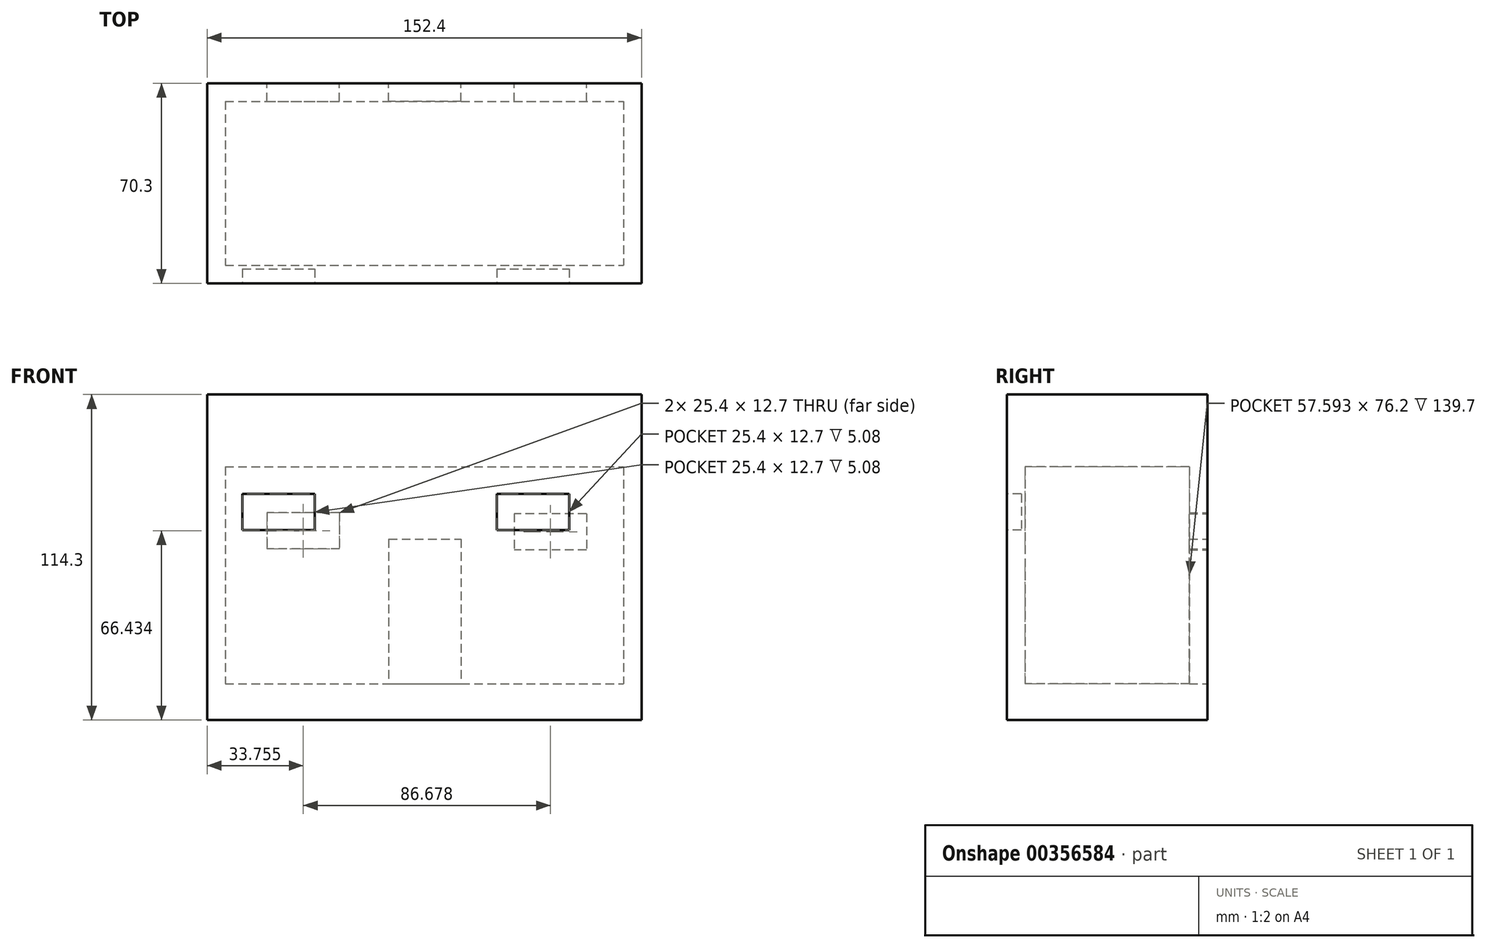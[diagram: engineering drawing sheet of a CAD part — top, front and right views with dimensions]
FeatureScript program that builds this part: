
annotation { "Feature Type Name" : "Feature", "Feature Type Description" : "" }
export const myFeature = defineFeature(function(context is Context, id is Id, definition is map)
    precondition{}
    {
        {
            var Q0;
            Q0=qCreatedBy(makeId("Top.planeOp"),FACE);
            var sketch = newSketch(context, id + "F0", { "sketchPlane" : qUnion([Q0])});
            skLineSegment(sketch, "E0.bottom", {"start": v(76.2, 35.15) * mm, "end": v(-76.2, 35.15) * mm});
            skLineSegment(sketch, "E0.top", {"start": v(76.2, -35.15) * mm, "end": v(-76.2, -35.15) * mm});
            skLineSegment(sketch, "E0.left", {"start": v(76.2, 35.15) * mm, "end": v(76.2, -35.15) * mm});
            skLineSegment(sketch, "E0.right", {"start": v(-76.2, 35.15) * mm, "end": v(-76.2, -35.15) * mm});
            skPoint(sketch, "E0.middle", {"position": v(0, 0) * mm});
            skSolve(sketch);
        }
        {
            var Q0;
            Q0 = qSketchRegion(id + "F0", true);
            extrude(context, id + "F1", {"entities" : qUnion([Q0]), "depth" : 12.7 * mm});
        }
        {
            var Q0;
            Q0=makeQuery(id+"F1.opExtrude","CAP_FACE",FACE,{"disambiguationData":[OSD([sQuery(id+"F0.wireOp",EDGE,"E0.bottom"),sQuery(id+"F0.wireOp",EDGE,"E0.top"),sQuery(id+"F0.wireOp",EDGE,"E0.left"),sQuery(id+"F0.wireOp",EDGE,"E0.right")])],"isStart":false});
            var sketch = newSketch(context, id + "F2", { "sketchPlane" : qUnion([Q0])});
            skLineSegment(sketch, "E1.bottom", {"start": v(-76.2, 35.15) * mm, "end": v(76.2, 35.15) * mm});
            skLineSegment(sketch, "E1.top", {"start": v(-76.2, 28.8) * mm, "end": v(76.2, 28.8) * mm});
            skLineSegment(sketch, "E1.left", {"start": v(-76.2, 35.15) * mm, "end": v(-76.2, 28.8) * mm});
            skLineSegment(sketch, "E1.right", {"start": v(76.2, 35.15) * mm, "end": v(76.2, 28.8) * mm});
            skLineSegment(sketch, "E2.bottom", {"start": v(-76.2, -28.8) * mm, "end": v(76.2, -28.8) * mm});
            skLineSegment(sketch, "E2.top", {"start": v(-76.2, -35.15) * mm, "end": v(76.2, -35.15) * mm});
            skLineSegment(sketch, "E2.left", {"start": v(-76.2, -28.8) * mm, "end": v(-76.2, -35.15) * mm});
            skLineSegment(sketch, "E2.right", {"start": v(76.2, -28.8) * mm, "end": v(76.2, -35.15) * mm});
            skLineSegment(sketch, "E3.bottom", {"start": v(-70.56, 35.15) * mm, "end": v(-63.18, 35.15) * mm});
            skLineSegment(sketch, "E4.bottom", {"start": v(-76.2, 28.8) * mm, "end": v(-69.85, 28.8) * mm});
            skLineSegment(sketch, "E4.top", {"start": v(-76.2, -28.8) * mm, "end": v(-69.85, -28.8) * mm});
            skLineSegment(sketch, "E4.left", {"start": v(-76.2, 28.8) * mm, "end": v(-76.2, -28.8) * mm});
            skLineSegment(sketch, "E4.right", {"start": v(-69.85, 28.8) * mm, "end": v(-69.85, -28.8) * mm});
            skLineSegment(sketch, "E5.bottom", {"start": v(76.2, 28.8) * mm, "end": v(69.85, 28.8) * mm});
            skLineSegment(sketch, "E5.top", {"start": v(76.2, -28.8) * mm, "end": v(69.85, -28.8) * mm});
            skLineSegment(sketch, "E5.left", {"start": v(76.2, 28.8) * mm, "end": v(76.2, -28.8) * mm});
            skLineSegment(sketch, "E5.right", {"start": v(69.85, 28.8) * mm, "end": v(69.85, -28.8) * mm});
            skSolve(sketch);
        }
        {
            var Q0;
            Q0 = qSketchRegion(id + "F2", true);
            extrude(context, id + "F3", {"entities" : qUnion([Q0]), "operationType" : NewBodyOperationType.ADD, "depth" : 76.2 * mm});
        }
        {
            var Q0;
            Q0=makeQuery(id+"F3.boolean.opBoolean","MERGE",FACE,{"derivedFrom":[makeQuery(id+"F1.opExtrude","SWEPT_FACE",FACE,{"disambiguationData":[OSD([sQuery(id+"F0.wireOp",EDGE,"E0.bottom")])]}),makeQuery(id+"F3.opExtrude","SWEPT_FACE",FACE,{"disambiguationData":[OSD([sQuery(id+"F2.wireOp",EDGE,"E1.bottom"),sQuery(id+"F2.wireOp",EDGE,"E3.bottom")])]})]});
            var sketch = newSketch(context, id + "F4", { "sketchPlane" : qUnion([Q0])});
            skLineSegment(sketch, "E6.bottom", {"start": v(12.47, 63.5) * mm, "end": v(-12.93, 63.5) * mm});
            skLineSegment(sketch, "E6.top", {"start": v(12.47, 12.7) * mm, "end": v(-12.93, 12.7) * mm});
            skLineSegment(sketch, "E6.left", {"start": v(12.47, 63.5) * mm, "end": v(12.47, 12.7) * mm});
            skLineSegment(sketch, "E6.right", {"start": v(-12.93, 63.5) * mm, "end": v(-12.93, 12.7) * mm});
            skLineSegment(sketch, "E7.bottom", {"start": v(-56.93, 72.46) * mm, "end": v(-31.53, 72.46) * mm});
            skLineSegment(sketch, "E7.top", {"start": v(-56.93, 59.76) * mm, "end": v(-31.53, 59.76) * mm});
            skLineSegment(sketch, "E7.left", {"start": v(-56.93, 72.46) * mm, "end": v(-56.93, 59.76) * mm});
            skLineSegment(sketch, "E7.right", {"start": v(-31.53, 72.46) * mm, "end": v(-31.53, 59.76) * mm});
            skLineSegment(sketch, "E8.bottom", {"start": v(29.75, 72.78) * mm, "end": v(55.15, 72.78) * mm});
            skLineSegment(sketch, "E8.top", {"start": v(29.75, 60.08) * mm, "end": v(55.15, 60.08) * mm});
            skLineSegment(sketch, "E8.left", {"start": v(29.75, 72.78) * mm, "end": v(29.75, 60.08) * mm});
            skLineSegment(sketch, "E8.right", {"start": v(55.15, 72.78) * mm, "end": v(55.15, 60.08) * mm});
            skSolve(sketch);
        }
        {
            var Q0;
            Q0 = qSketchRegion(id + "F4", true);
            extrude(context, id + "F5", {"entities" : qUnion([Q0]), "operationType" : NewBodyOperationType.REMOVE, "endBound" : BoundingType.UP_TO_NEXT, "oppositeDirection" : true, "depth" : 25.4 * mm});
        }
        {
            var Q0;
            Q0=makeQuery(id+"F3.boolean.opBoolean","MERGE",FACE,{"derivedFrom":[makeQuery(id+"F1.opExtrude","SWEPT_FACE",FACE,{"disambiguationData":[OSD([sQuery(id+"F0.wireOp",EDGE,"E0.top")])]}),makeQuery(id+"F3.opExtrude","SWEPT_FACE",FACE,{"disambiguationData":[OSD([sQuery(id+"F2.wireOp",EDGE,"E2.top")])]})]});
            var sketch = newSketch(context, id + "F6", { "sketchPlane" : qUnion([Q0])});
            skLineSegment(sketch, "E9.bottom", {"start": v(-63.78, 79.36) * mm, "end": v(-38.38, 79.36) * mm});
            skLineSegment(sketch, "E9.top", {"start": v(-63.78, 66.66) * mm, "end": v(-38.38, 66.66) * mm});
            skLineSegment(sketch, "E9.left", {"start": v(-63.78, 79.36) * mm, "end": v(-63.78, 66.66) * mm});
            skLineSegment(sketch, "E9.right", {"start": v(-38.38, 79.36) * mm, "end": v(-38.38, 66.66) * mm});
            skLineSegment(sketch, "E10.bottom", {"start": v(25.43, 79.38) * mm, "end": v(50.83, 79.38) * mm});
            skLineSegment(sketch, "E10.top", {"start": v(25.43, 66.68) * mm, "end": v(50.83, 66.68) * mm});
            skLineSegment(sketch, "E10.left", {"start": v(25.43, 79.38) * mm, "end": v(25.43, 66.68) * mm});
            skLineSegment(sketch, "E10.right", {"start": v(50.83, 79.38) * mm, "end": v(50.83, 66.68) * mm});
            skLineSegment(sketch, "E11.bottom", {"start": v(-63.78, 79.57) * mm, "end": v(55.3, 79.57) * mm, "construction": true});
            skLineSegment(sketch, "E11.left", {"start": v(-63.78, 79.57) * mm, "end": v(-63.78, 77.93) * mm, "construction": true});
            skLineSegment(sketch, "E11.right", {"start": v(55.3, 79.57) * mm, "end": v(55.3, 79.38) * mm, "construction": true});
            skSolve(sketch);
        }
        {
            var Q0;
            Q0=makeQuery(id+"F6.imprint","IMPRINT",FACE,{"disambiguationData":[TD([[makeQuery(id+"F6.imprint","IMPRINT",EDGE,{"derivedFrom":sQuery(id+"F6.wireOp",EDGE,"E9.bottom")}),-1.0]])]});
            var Q1;
            Q1=makeQuery(id+"F6.imprint","IMPRINT",FACE,{"disambiguationData":[TD([[makeQuery(id+"F6.imprint","IMPRINT",EDGE,{"derivedFrom":sQuery(id+"F6.wireOp",EDGE,"E10.bottom")}),-1.0]])]});
            extrude(context, id + "F7", {"entities" : qUnion([Q0, Q1]), "operationType" : NewBodyOperationType.REMOVE, "oppositeDirection" : true, "depth" : 5.08 * mm});
        }
        {
            var Q0;
            Q0=makeQuery(id+"F3.opExtrude","CAP_FACE",FACE,{"disambiguationData":[OSD([sQuery(id+"F2.wireOp",EDGE,"E1.bottom"),sQuery(id+"F2.wireOp",EDGE,"E1.top"),sQuery(id+"F2.wireOp",EDGE,"E1.left"),sQuery(id+"F2.wireOp",EDGE,"E1.right"),sQuery(id+"F2.wireOp",EDGE,"E2.bottom"),sQuery(id+"F2.wireOp",EDGE,"E2.top"),sQuery(id+"F2.wireOp",EDGE,"E2.left"),sQuery(id+"F2.wireOp",EDGE,"E2.right"),sQuery(id+"F2.wireOp",EDGE,"E3.bottom"),sQuery(id+"F2.wireOp",EDGE,"E4.left"),sQuery(id+"F2.wireOp",EDGE,"E4.right"),sQuery(id+"F2.wireOp",EDGE,"E5.left"),sQuery(id+"F2.wireOp",EDGE,"E5.right")])],"isStart":false});
            var sketch = newSketch(context, id + "F8", { "sketchPlane" : qUnion([Q0])});
            skLineSegment(sketch, "E12.bottom", {"start": v(-76.2, 35.15) * mm, "end": v(76.2, 35.15) * mm});
            skLineSegment(sketch, "E12.top", {"start": v(-76.2, -35.15) * mm, "end": v(76.2, -35.15) * mm});
            skLineSegment(sketch, "E12.left", {"start": v(-76.2, 35.15) * mm, "end": v(-76.2, -35.15) * mm});
            skLineSegment(sketch, "E12.right", {"start": v(76.2, 35.15) * mm, "end": v(76.2, -35.15) * mm});
            skSolve(sketch);
        }
        {
            var Q0;
            Q0 = qSketchRegion(id + "F8", true);
            extrude(context, id + "F9", {"entities" : qUnion([Q0]), "operationType" : NewBodyOperationType.ADD, "depth" : 25.4 * mm});
        }
    });
